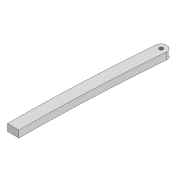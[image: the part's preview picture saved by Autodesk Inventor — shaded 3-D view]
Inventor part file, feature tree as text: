
AUTODESK INVENTOR PART (.ipt)
format: ipt  version: 2022 (Build 260153000, 153)  size: 101,376 bytes
history: native  units: mm
features: extrude x2, sketch x2
ambient origin geometry x8: Origin, YZ Plane, XZ Plane, XY Plane, X Axis, Y Axis, Z Axis, Center Point
bodies: Solid1 (feature_tree)
feature tree (4):
  extrude  "Extrusion1"  Depth=3.3mm
  extrude  "Extrusion2"  Depth=253.429mm
  sketch  "Sketch1"  dims[d0=3.3mm d1=3.3mm]
  sketch  "Sketch2"  dims[d2=10.0mm d3=253.429mm d6=6.0mm d7=0.0mm d16=1500.0mm d17=1500.0mm d18=10.0mm d19=0.0mm]
